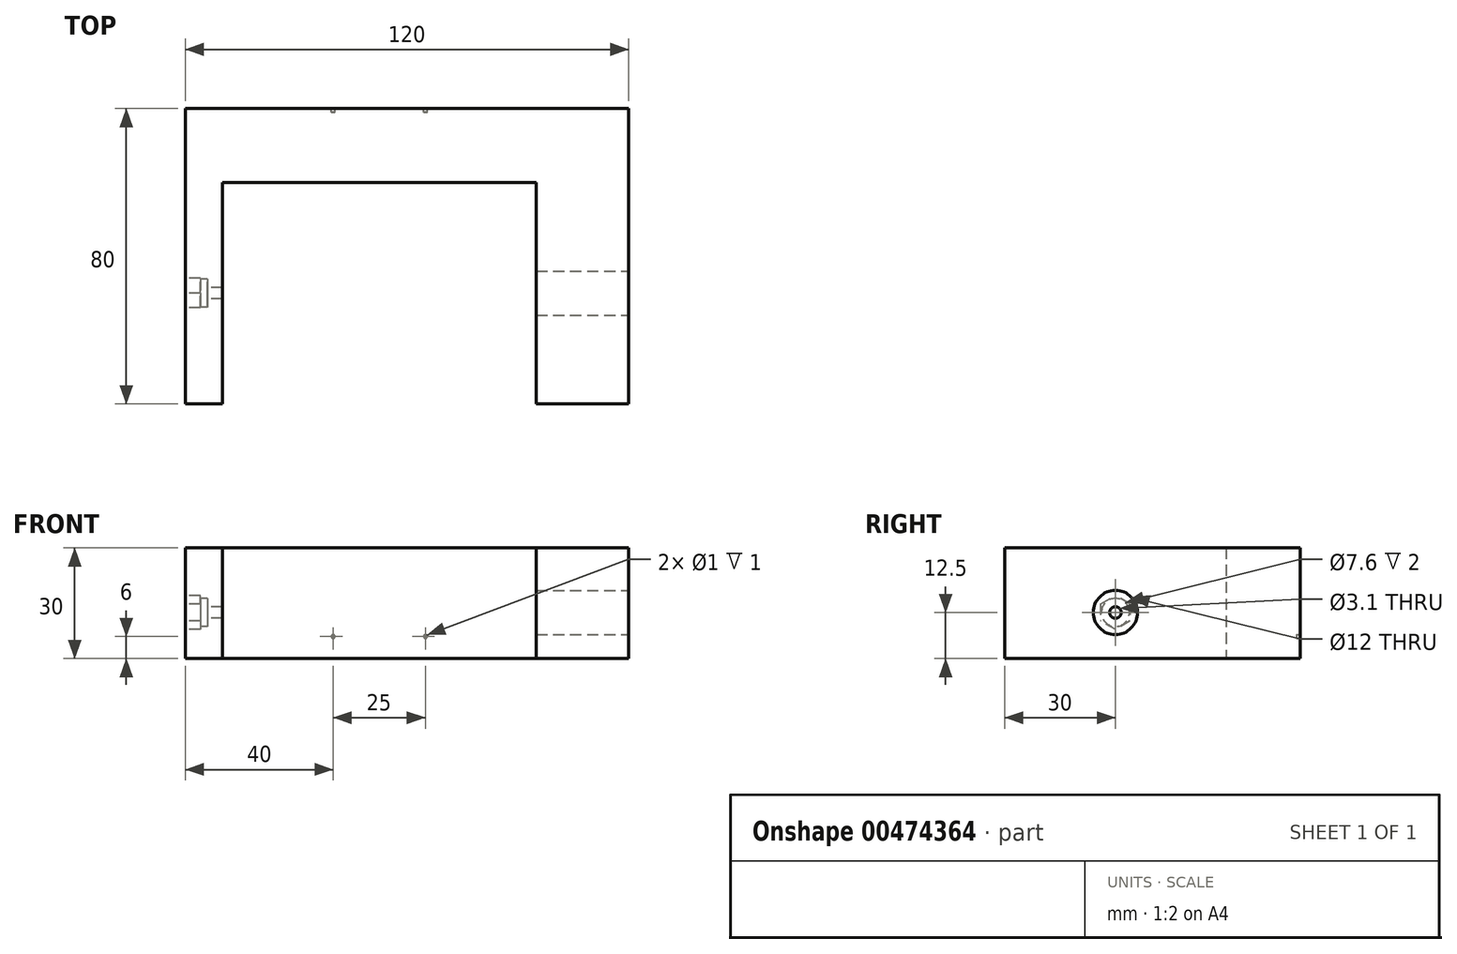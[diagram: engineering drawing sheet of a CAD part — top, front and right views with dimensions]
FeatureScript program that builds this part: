
annotation { "Feature Type Name" : "Feature", "Feature Type Description" : "" }
export const myFeature = defineFeature(function(context is Context, id is Id, definition is map)
    precondition{}
    {
        {
            var Q0;
            Q0=qCreatedBy(makeId("Top.planeOp"),FACE);
            var sketch = newSketch(context, id + "F0", { "sketchPlane" : qUnion([Q0])});
            skLineSegment(sketch, "E0.bottom", {"start": v(-60, -40) * mm, "end": v(60, -40) * mm});
            skLineSegment(sketch, "E0.top", {"start": v(-60, 40) * mm, "end": v(60, 40) * mm});
            skLineSegment(sketch, "E0.left", {"start": v(-60, -40) * mm, "end": v(-60, 40) * mm});
            skLineSegment(sketch, "E0.right", {"start": v(60, -40) * mm, "end": v(60, 40) * mm});
            skPoint(sketch, "E0.middle", {"position": v(0, 0) * mm});
            skSolve(sketch);
        }
        {
            var Q0;
            Q0 = qSketchRegion(id + "F0", true);
            extrude(context, id + "F1", {"entities" : qUnion([Q0]), "depth" : 30 * mm});
        }
        {
            var Q0;
            Q0=makeQuery(id+"F1.opExtrude","SWEPT_FACE",FACE,{"disambiguationData":[OSD([sQuery(id+"F0.wireOp",EDGE,"E0.left")])]});
            var sketch = newSketch(context, id + "F2", { "sketchPlane" : qUnion([Q0])});
            skPoint(sketch, "E1.endSnap0", {"position": v(0, 0) * mm});
            skLineSegment(sketch, "E2", {"start": v(-40, 15) * mm, "end": v(-20, 15) * mm, "construction": true});
            skLineSegment(sketch, "E3", {"start": v(40, 0) * mm, "end": v(40, 12.5) * mm, "construction": true});
            skLineSegment(sketch, "E4", {"start": v(40, 12.5) * mm, "end": v(10, 12.5) * mm, "construction": true});
            skLineSegment(sketch, "E5", {"start": v(10, 12.5) * mm, "end": v(10, 17.12) * mm, "construction": true});
            skLineSegment(sketch, "E6", {"start": v(10, 12.5) * mm, "end": v(14, 14.8) * mm, "construction": true});
            skLineSegment(sketch, "E7.MirrorCS", {"start": v(10, 12.5) * mm, "end": v(14, 10.19) * mm, "construction": true});
            skLineSegment(sketch, "E8.MirrorCS", {"start": v(10, 12.5) * mm, "end": v(10, 7.88) * mm, "construction": true});
            skLineSegment(sketch, "E9.MirrorCS", {"start": v(10, 12.5) * mm, "end": v(6, 10.19) * mm, "construction": true});
            skLineSegment(sketch, "E10.MirrorCS", {"start": v(10, 12.5) * mm, "end": v(6, 14.8) * mm, "construction": true});
            skLineSegment(sketch, "E11", {"start": v(6, 14.8) * mm, "end": v(10, 17.12) * mm});
            skLineSegment(sketch, "E12", {"start": v(6, 14.8) * mm, "end": v(6, 10.19) * mm});
            skLineSegment(sketch, "E13", {"start": v(6, 10.19) * mm, "end": v(10, 7.88) * mm});
            skLineSegment(sketch, "E14", {"start": v(10, 7.88) * mm, "end": v(14, 10.2) * mm});
            skLineSegment(sketch, "E15", {"start": v(14, 14.8) * mm, "end": v(14, 10.2) * mm});
            skLineSegment(sketch, "E16", {"start": v(14, 14.8) * mm, "end": v(10, 17.12) * mm});
            skLineSegment(sketch, "E17", {"start": v(6, 14.8) * mm, "end": v(14, 14.8) * mm, "construction": true});
            skSolve(sketch);
        }
        {
            var Q0;
            Q0=qCreatedBy(makeId("Top.planeOp"),FACE);
            var sketch = newSketch(context, id + "F3", { "sketchPlane" : qUnion([Q0])});
            skLineSegment(sketch, "E18.right", {"start": v(35, 20) * mm, "end": v(35, 20) * mm});
            skLineSegment(sketch, "E19", {"start": v(-50, 20) * mm, "end": v(35, 20) * mm});
            skLineSegment(sketch, "E20", {"start": v(-50, 20) * mm, "end": v(-50, -40) * mm});
            skLineSegment(sketch, "E21", {"start": v(-50, -40) * mm, "end": v(35, -40) * mm});
            skLineSegment(sketch, "E22", {"start": v(35, 20) * mm, "end": v(35, -40) * mm});
            skSolve(sketch);
        }
        {
            var Q0;
            Q0 = qSketchRegion(id + "F3", true);
            var Q1;
            Q1=makeQuery(id+"F1.opExtrude","CAP_FACE",FACE,{"disambiguationData":[OSD([sQuery(id+"F0.wireOp",EDGE,"E0.bottom"),sQuery(id+"F0.wireOp",EDGE,"E0.top"),sQuery(id+"F0.wireOp",EDGE,"E0.left"),sQuery(id+"F0.wireOp",EDGE,"E0.right")])],"isStart":false});
            extrude(context, id + "F4", {"entities" : qUnion([Q0]), "operationType" : NewBodyOperationType.REMOVE, "endBound" : BoundingType.UP_TO_SURFACE, "endBoundEntityFace" : qUnion([Q1]), "depth" : 25 * mm});
        }
        {
            var Q0;
            Q0 = qSketchRegion(id + "F2", true);
            extrude(context, id + "F5", {"entities" : qUnion([Q0]), "operationType" : NewBodyOperationType.REMOVE, "oppositeDirection" : true, "depth" : 4 * mm});
        }
        {
            var Q0;
            Q0=makeQuery(id+"F5.boolean.opBoolean","COPY",FACE,{"derivedFrom":makeQuery(id+"F5.opExtrude","CAP_FACE",FACE,{"disambiguationData":[OSD([sQuery(id+"F2.wireOp",EDGE,"E11"),sQuery(id+"F2.wireOp",EDGE,"E12"),sQuery(id+"F2.wireOp",EDGE,"E13"),sQuery(id+"F2.wireOp",EDGE,"E14"),sQuery(id+"F2.wireOp",EDGE,"E15"),sQuery(id+"F2.wireOp",EDGE,"E16")])],"isStart":false})});
            var sketch = newSketch(context, id + "F6", { "sketchPlane" : qUnion([Q0])});
            skCircle(sketch, "E23", {"center": v(10, 12.5) * mm, "radius": 3.8 * mm});
            skSolve(sketch);
        }
        {
            var Q0;
            Q0 = qSketchRegion(id + "F6", true);
            extrude(context, id + "F7", {"entities" : qUnion([Q0]), "operationType" : NewBodyOperationType.REMOVE, "oppositeDirection" : true, "depth" : 2 * mm});
        }
        {
            var Q0;
            Q0=makeQuery(id+"F7.boolean.opBoolean","COPY",FACE,{"derivedFrom":makeQuery(id+"F7.opExtrude","CAP_FACE",FACE,{"disambiguationData":[OSD([sQuery(id+"F6.wireOp",EDGE,"E23")])],"isStart":false})});
            var sketch = newSketch(context, id + "F8", { "sketchPlane" : qUnion([Q0])});
            skLineSegment(sketch, "E24", {"start": v(10, 20.63) * mm, "end": v(10, 4.75) * mm, "construction": true});
            skLineSegment(sketch, "E25", {"start": v(3.02, 8.45) * mm, "end": v(16.9, 16.52) * mm, "construction": true});
            skCircle(sketch, "E26", {"center": v(10, 12.5) * mm, "radius": 1.55 * mm});
            skSolve(sketch);
        }
        {
            var Q0;
            Q0 = qSketchRegion(id + "F8", true);
            extrude(context, id + "F9", {"entities" : qUnion([Q0]), "operationType" : NewBodyOperationType.REMOVE, "oppositeDirection" : true, "depth" : 7 * mm});
        }
        {
            var Q0;
            Q0=makeQuery(id+"F1.opExtrude","SWEPT_FACE",FACE,{"disambiguationData":[OSD([sQuery(id+"F0.wireOp",EDGE,"E0.right")])]});
            var sketch = newSketch(context, id + "F10", { "sketchPlane" : qUnion([Q0])});
            skLineSegment(sketch, "E27", {"start": v(-40, 0) * mm, "end": v(-40, 12.5) * mm, "construction": true});
            skLineSegment(sketch, "E28", {"start": v(-40, 12.5) * mm, "end": v(-10, 12.5) * mm, "construction": true});
            skCircle(sketch, "E29", {"center": v(-10, 12.5) * mm, "radius": 6 * mm});
            skSolve(sketch);
        }
        {
            var Q0;
            Q0=makeQuery(id+"F1.opExtrude","SWEPT_FACE",FACE,{"disambiguationData":[OSD([sQuery(id+"F0.wireOp",EDGE,"E0.top")])]});
            var sketch = newSketch(context, id + "F11", { "sketchPlane" : qUnion([Q0])});
            skPoint(sketch, "E30.endSnap0", {"position": v(0, 0) * mm});
            skLineSegment(sketch, "E31", {"start": v(-60, 6) * mm, "end": v(-35, 6) * mm, "construction": true});
            skPoint(sketch, "E32", {"position": v(-35, 6) * mm});
            skLineSegment(sketch, "E33", {"start": v(60, 6) * mm, "end": v(50, 6) * mm, "construction": true});
            skLineSegment(sketch, "E34", {"start": v(-5, 6) * mm, "end": v(20, 6) * mm, "construction": true});
            skCircle(sketch, "E35", {"center": v(20, 6) * mm, "radius": 0.5 * mm});
            skLineSegment(sketch, "E36", {"start": v(20, 6) * mm, "end": v(50, 6) * mm, "construction": true});
            skLineSegment(sketch, "E37", {"start": v(0, 0) * mm, "end": v(-5, 0) * mm, "construction": true});
            skLineSegment(sketch, "E38", {"start": v(0, 0) * mm, "end": v(0, 6) * mm, "construction": true});
            skCircle(sketch, "E39", {"center": v(-5, 6) * mm, "radius": 0.5 * mm});
            skLineSegment(sketch, "E40", {"start": v(-35, 6) * mm, "end": v(-5, 6) * mm, "construction": true});
            skSolve(sketch);
        }
        {
            var Q0;
            Q0 = qSketchRegion(id + "F10", true);
            var Q1;
            Q1=makeQuery(id+"F4.boolean.opBoolean","COPY",FACE,{"derivedFrom":makeQuery(id+"F4.opExtrude","SWEPT_FACE",FACE,{"disambiguationData":[OSD([sQuery(id+"F3.wireOp",EDGE,"E22")])]})});
            extrude(context, id + "F12", {"entities" : qUnion([Q0]), "operationType" : NewBodyOperationType.REMOVE, "endBound" : BoundingType.UP_TO_SURFACE, "oppositeDirection" : true, "endBoundEntityFace" : qUnion([Q1]), "depth" : 25 * mm});
        }
        {
            var Q0;
            Q0 = qSketchRegion(id + "F11", true);
            var Q1;
            Q1=makeQuery(id+"F4.boolean.opBoolean","COPY",FACE,{"derivedFrom":makeQuery(id+"F4.opExtrude","SWEPT_FACE",FACE,{"disambiguationData":[OSD([sQuery(id+"F3.wireOp",EDGE,"E19")])]})});
            extrude(context, id + "F13", {"entities" : qUnion([Q0]), "operationType" : NewBodyOperationType.REMOVE, "oppositeDirection" : true, "endBoundEntityFace" : qUnion([Q1]), "depth" : 1 * mm});
        }
    });
